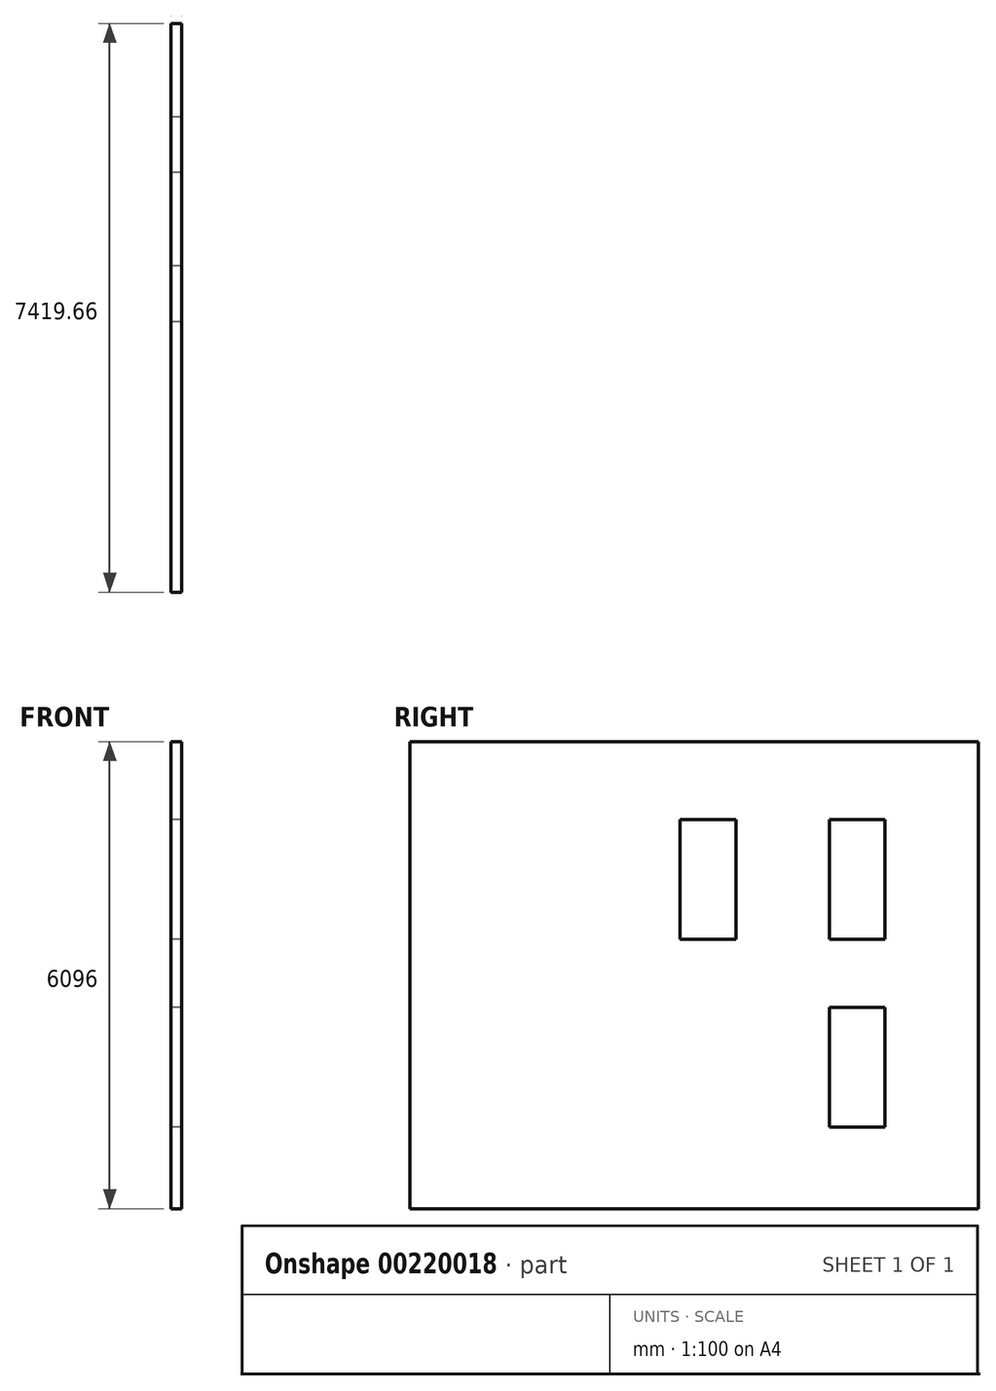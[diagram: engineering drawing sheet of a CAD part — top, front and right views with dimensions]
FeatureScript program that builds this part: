
annotation { "Feature Type Name" : "Feature", "Feature Type Description" : "" }
export const myFeature = defineFeature(function(context is Context, id is Id, definition is map)
    precondition{}
    {
        {
            var Q0;
            Q0=qCreatedBy(makeId("Right.planeOp"),FACE);
            var sketch = newSketch(context, id + "F0", { "sketchPlane" : qUnion([Q0])});
            skLineSegment(sketch, "E0.bottom", {"start": v(0, 0) * mm, "end": v(7419.66, 0) * mm});
            skLineSegment(sketch, "E0.top", {"start": v(0, 6096) * mm, "end": v(7419.66, 6096) * mm});
            skLineSegment(sketch, "E0.left", {"start": v(0, 0) * mm, "end": v(0, 6096) * mm});
            skLineSegment(sketch, "E0.right", {"start": v(7419.66, 0) * mm, "end": v(7419.66, 6096) * mm});
            skSolve(sketch);
        }
        {
            var Q0;
            Q0=makeQuery(id+"F0.imprint","IMPRINT",FACE,{"disambiguationData":[TD([[makeQuery(id+"F0.imprint","IMPRINT",EDGE,{"derivedFrom":sQuery(id+"F0.wireOp",EDGE,"E0.bottom")}),1.0]])]});
            extrude(context, id + "F1", {"entities" : qUnion([Q0]), "depth" : 138.27 * mm});
        }
        {
            var Q0;
            Q0=qCreatedBy(makeId("Front.planeOp"),FACE);
            var sketch = newSketch(context, id + "F2", { "sketchPlane" : qUnion([Q0])});
            skLineSegment(sketch, "E1", {"start": v(0, 6096) * mm, "end": v(2933.7, 10515.6) * mm, "construction": true});
            skLineSegment(sketch, "E2", {"start": v(0, 6096) * mm, "end": v(-609.6, 5177.64) * mm, "construction": true});
            skSolve(sketch);
        }
        {
            var Q0;
            Q0=sQuery(id+"F2.wireOp",VERTEX,"E2.end");
            var Q1;
            Q1=makeQuery(id+"F1.opExtrude","CAP_FACE",FACE,{"disambiguationData":[OSD([sQuery(id+"F0.wireOp",EDGE,"E0.bottom"),sQuery(id+"F0.wireOp",EDGE,"E0.top"),sQuery(id+"F0.wireOp",EDGE,"E0.left"),sQuery(id+"F0.wireOp",EDGE,"E0.right")])],"isStart":true});
            cPlane(context, id + "F3", {"entities" : qUnion([Q0, Q1]), "cplaneType" : CPlaneType.PLANE_POINT, "offset" : 25.4 * mm, "width" : 152.4 * mm, "height" : 152.4 * mm});
        }
        {
            var Q0;
            Q0=qCreatedBy(id+"F3.planeOp",FACE);
            var sketch = newSketch(context, id + "F4", { "sketchPlane" : qUnion([Q0])});
            skLineSegment(sketch, "E3", {"start": v(0, 5177.64) * mm, "end": v(-8419.14, 5177.64) * mm, "construction": true});
            skSolve(sketch);
        }
        {
            var Q0;
            Q0=makeQuery(id+"F1.opExtrude","CAP_FACE",FACE,{"disambiguationData":[OSD([sQuery(id+"F0.wireOp",EDGE,"E0.bottom"),sQuery(id+"F0.wireOp",EDGE,"E0.top"),sQuery(id+"F0.wireOp",EDGE,"E0.left"),sQuery(id+"F0.wireOp",EDGE,"E0.right")])],"isStart":true});
            var sketch = newSketch(context, id + "F5", { "sketchPlane" : qUnion([Q0])});
            skLineSegment(sketch, "E4.bottom", {"start": v(-6200.46, 5076.04) * mm, "end": v(-5474.8, 5076.04) * mm});
            skLineSegment(sketch, "E4.top", {"start": v(-6200.46, 3516.34) * mm, "end": v(-5474.8, 3516.34) * mm});
            skLineSegment(sketch, "E4.left", {"start": v(-6200.46, 5076.04) * mm, "end": v(-6200.46, 3516.34) * mm});
            skLineSegment(sketch, "E4.right", {"start": v(-5474.8, 5076.04) * mm, "end": v(-5474.8, 3516.34) * mm});
            skLineSegment(sketch, "E5.bottom", {"start": v(-4255.6, 5076.04) * mm, "end": v(-3529.96, 5076.04) * mm});
            skLineSegment(sketch, "E5.top", {"start": v(-4255.6, 3516.34) * mm, "end": v(-3529.96, 3516.34) * mm});
            skLineSegment(sketch, "E5.left", {"start": v(-4255.6, 5076.04) * mm, "end": v(-4255.6, 3516.34) * mm});
            skLineSegment(sketch, "E5.right", {"start": v(-3529.96, 5076.04) * mm, "end": v(-3529.96, 3516.34) * mm});
            skLineSegment(sketch, "E6.bottom", {"start": v(-6200.46, 2626.5) * mm, "end": v(-5474.8, 2626.5) * mm});
            skLineSegment(sketch, "E6.top", {"start": v(-6200.46, 1066.8) * mm, "end": v(-5474.8, 1066.8) * mm});
            skLineSegment(sketch, "E6.left", {"start": v(-6200.46, 2626.5) * mm, "end": v(-6200.46, 1066.8) * mm});
            skLineSegment(sketch, "E6.right", {"start": v(-5474.8, 2626.5) * mm, "end": v(-5474.8, 1066.8) * mm});
            skSolve(sketch);
        }
        {
            var Q0;
            Q0=makeQuery(id+"F5.imprint","IMPRINT",FACE,{"disambiguationData":[TD([[makeQuery(id+"F5.imprint","IMPRINT",EDGE,{"derivedFrom":sQuery(id+"F5.wireOp",EDGE,"E6.bottom")}),-1.0]])]});
            var Q1;
            Q1=makeQuery(id+"F5.imprint","IMPRINT",FACE,{"disambiguationData":[TD([[makeQuery(id+"F5.imprint","IMPRINT",EDGE,{"derivedFrom":sQuery(id+"F5.wireOp",EDGE,"E4.bottom")}),-1.0]])]});
            var Q2;
            Q2=makeQuery(id+"F5.imprint","IMPRINT",FACE,{"disambiguationData":[TD([[makeQuery(id+"F5.imprint","IMPRINT",EDGE,{"derivedFrom":sQuery(id+"F5.wireOp",EDGE,"E5.bottom")}),-1.0]])]});
            extrude(context, id + "F6", {"entities" : qUnion([Q0, Q1, Q2]), "operationType" : NewBodyOperationType.REMOVE, "endBound" : BoundingType.THROUGH_ALL, "oppositeDirection" : true, "depth" : 25.4 * mm});
        }
    });
